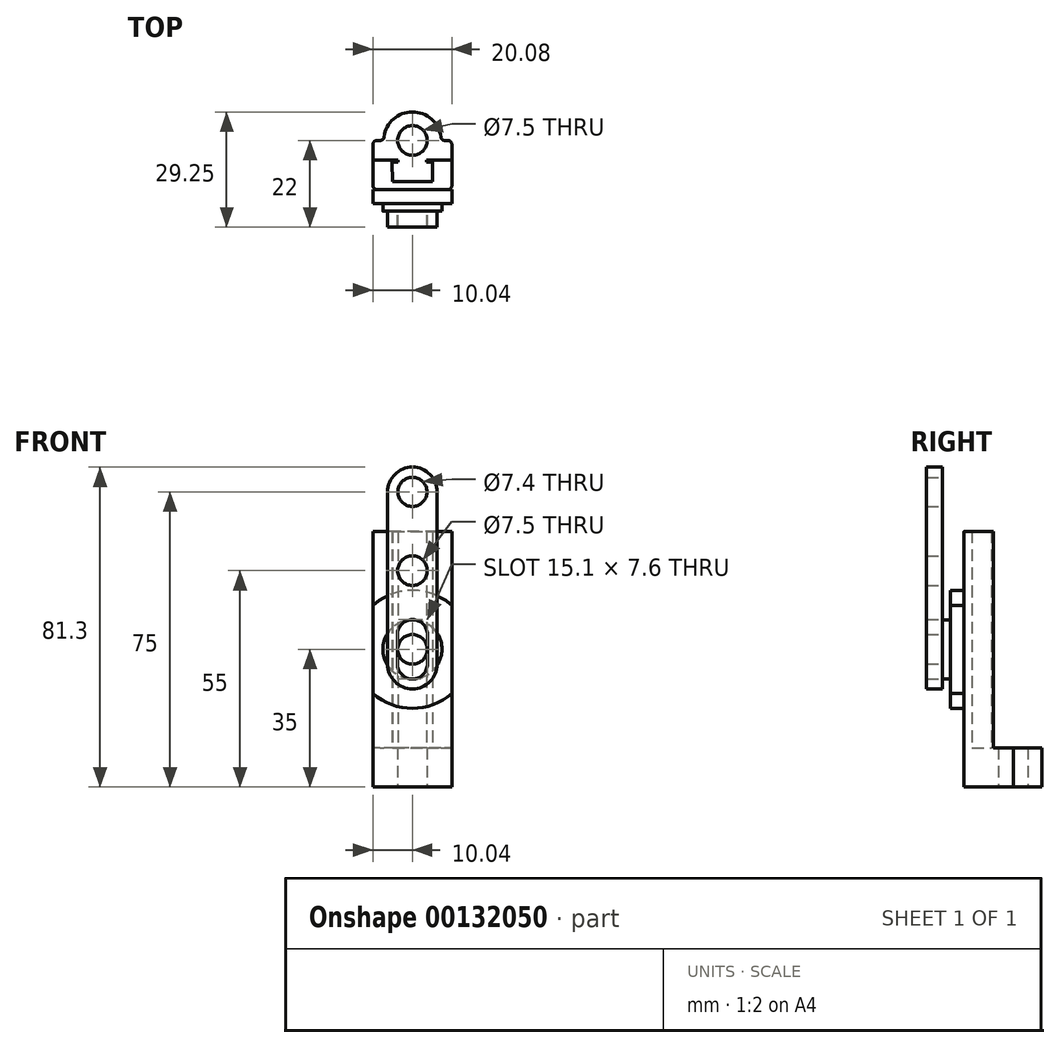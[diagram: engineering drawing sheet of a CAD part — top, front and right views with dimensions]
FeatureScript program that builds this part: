
annotation { "Feature Type Name" : "Feature", "Feature Type Description" : "" }
export const myFeature = defineFeature(function(context is Context, id is Id, definition is map)
    precondition{}
    {
        {
            var Q0;
            Q0=qCreatedBy(makeId("Top.planeOp"),FACE);
            var sketch = newSketch(context, id + "F0", { "sketchPlane" : qUnion([Q0])});
            skCircle(sketch, "E0", {"center": v(0, 0) * mm, "radius": 3.75 * mm});
            skArc(sketch, "E1.0", {"start": v(7.2, 0.88) * mm, "mid": v(0, 7.25) * mm, "end": v(-7.2, 0.88) * mm});
            skLineSegment(sketch, "E2.bottom", {"start": v(9, 0) * mm, "end": v(8.19, 0) * mm});
            skLineSegment(sketch, "E2.top", {"start": v(9, -12.5) * mm, "end": v(-9, -12.5) * mm});
            skLineSegment(sketch, "E2.left", {"start": v(10, -1) * mm, "end": v(10, -11.5) * mm});
            skLineSegment(sketch, "E2.right", {"start": v(-10, -1) * mm, "end": v(-10, -11.5) * mm});
            skLineSegment(sketch, "E3.trimOffspring", {"start": v(-8.19, 0) * mm, "end": v(-9, 0) * mm});
            skPoint(sketch, "E4.visualSharp", {"position": v(-7.25, 0) * mm});
            skArc(sketch, "E4.filletArc", {"start": v(-8.19, 0) * mm, "mid": v(-7.53, 0.25) * mm, "end": v(-7.2, 0.88) * mm});
            skPoint(sketch, "E5.visualSharp", {"position": v(7.25, 0) * mm});
            skArc(sketch, "E5.filletArc", {"start": v(7.2, 0.88) * mm, "mid": v(7.53, 0.25) * mm, "end": v(8.19, 0) * mm});
            skPoint(sketch, "E6.visualSharp", {"position": v(10, 0) * mm});
            skArc(sketch, "E6.filletArc", {"start": v(10, -1) * mm, "mid": v(9.7, -0.3) * mm, "end": v(9, 0) * mm});
            skPoint(sketch, "E7.visualSharp", {"position": v(-10, 0) * mm});
            skArc(sketch, "E7.filletArc", {"start": v(-9, 0) * mm, "mid": v(-9.7, -0.3) * mm, "end": v(-10, -1) * mm});
            skPoint(sketch, "E8.visualSharp", {"position": v(10, -12.5) * mm});
            skArc(sketch, "E8.filletArc", {"start": v(9, -12.5) * mm, "mid": v(9.7, -12.2) * mm, "end": v(10, -11.5) * mm});
            skPoint(sketch, "E9.visualSharp", {"position": v(-10, -12.5) * mm});
            skArc(sketch, "E9.filletArc", {"start": v(-10, -11.5) * mm, "mid": v(-9.7, -12.2) * mm, "end": v(-9, -12.5) * mm});
            skSolve(sketch);
        }
        {
            var Q0;
            Q0=makeQuery(id+"F0.imprint","IMPRINT",FACE,{"disambiguationData":[TD([[makeQuery(id+"F0.imprint","IMPRINT",EDGE,{"derivedFrom":sQuery(id+"F0.wireOp",EDGE,"E0")}),-1.0]])]});
            extrude(context, id + "F1", {"entities" : qUnion([Q0]), "depth" : 10 * mm});
        }
        {
            var Q0;
            Q0=makeQuery(id+"F1.opExtrude","CAP_FACE",FACE,{"disambiguationData":[OSD([sQuery(id+"F0.wireOp",EDGE,"E0"),sQuery(id+"F0.wireOp",EDGE,"E1.0"),sQuery(id+"F0.wireOp",EDGE,"E2.bottom"),sQuery(id+"F0.wireOp",EDGE,"E2.top"),sQuery(id+"F0.wireOp",EDGE,"E2.left"),sQuery(id+"F0.wireOp",EDGE,"E2.right"),sQuery(id+"F0.wireOp",EDGE,"E3.trimOffspring"),sQuery(id+"F0.wireOp",EDGE,"E4.filletArc"),sQuery(id+"F0.wireOp",EDGE,"E5.filletArc"),sQuery(id+"F0.wireOp",EDGE,"E6.filletArc"),sQuery(id+"F0.wireOp",EDGE,"E7.filletArc"),sQuery(id+"F0.wireOp",EDGE,"E8.filletArc"),sQuery(id+"F0.wireOp",EDGE,"E9.filletArc")])],"isStart":false});
            var sketch = newSketch(context, id + "F2", { "sketchPlane" : qUnion([Q0])});
            skLineSegment(sketch, "E10", {"start": v(3.6, -5) * mm, "end": v(10, -5) * mm});
            skLineSegment(sketch, "E11", {"start": v(10, -5) * mm, "end": v(10, -11.5) * mm});
            skPoint(sketch, "E12.visualSharp", {"position": v(10, -12.5) * mm});
            skArc(sketch, "E12.filletArc", {"start": v(9, -12.5) * mm, "mid": v(9.7, -12.2) * mm, "end": v(10, -11.5) * mm});
            skLineSegment(sketch, "E13.MirrorCS", {"start": v(-10, -5) * mm, "end": v(-10, -11.5) * mm});
            skArc(sketch, "E14.MirrorCS", {"start": v(-9, -12.5) * mm, "mid": v(-9.7, -12.2) * mm, "end": v(-10, -11.5) * mm});
            skLineSegment(sketch, "E15", {"start": v(-9, -12.5) * mm, "end": v(9, -12.5) * mm});
            skLineSegment(sketch, "E16", {"start": v(3.6, -5) * mm, "end": v(3.6, -5.5) * mm});
            skLineSegment(sketch, "E17", {"start": v(3.6, -5.5) * mm, "end": v(5.14, -5.5) * mm});
            skPoint(sketch, "E18.orphan", {"position": v(0, -5) * mm});
            skLineSegment(sketch, "E19", {"start": v(5.05, -10.5) * mm, "end": v(5.14, -5.5) * mm});
            skLineSegment(sketch, "E20.MirrorCS", {"start": v(-5.05, -10.5) * mm, "end": v(-5.14, -5.5) * mm});
            skLineSegment(sketch, "E21.MirrorCS", {"start": v(-3.6, -5.5) * mm, "end": v(-5.14, -5.5) * mm});
            skLineSegment(sketch, "E22.MirrorCS", {"start": v(-3.6, -5) * mm, "end": v(-10, -5) * mm});
            skLineSegment(sketch, "E23.MirrorCS", {"start": v(-3.6, -5) * mm, "end": v(-3.6, -5.5) * mm});
            skLineSegment(sketch, "E24", {"start": v(-5.05, -10.5) * mm, "end": v(5.05, -10.5) * mm});
            skSolve(sketch);
        }
        {
            var Q0;
            Q0 = qSketchRegion(id + "F2", true);
            extrude(context, id + "F3", {"entities" : qUnion([Q0]), "operationType" : NewBodyOperationType.ADD, "depth" : 55 * mm});
        }
        {
            var Q0;
            Q0=makeQuery(id+"F3.boolean.opBoolean","MERGE",FACE,{"derivedFrom":[makeQuery(id+"F1.opExtrude","SWEPT_FACE",FACE,{"disambiguationData":[OSD([sQuery(id+"F0.wireOp",EDGE,"E2.top")])]}),makeQuery(id+"F3.opExtrude","SWEPT_FACE",FACE,{"disambiguationData":[OSD([sQuery(id+"F2.wireOp",EDGE,"rY1W6HYS-8gYD-yjMk-udCq-DS8X7DJZpoX9")])]}),makeQuery(id+"F3.opExtrude","SWEPT_FACE",FACE,{"disambiguationData":[OSD([sQuery(id+"F2.wireOp",EDGE,"4e3df5a9-557a-405f-80d9-8388369b6b7d0.MirrorCS")])]})]});
            var sketch = newSketch(context, id + "F4", { "sketchPlane" : qUnion([Q0])});
            skLineSegment(sketch, "E25", {"start": v(0, 0) * mm, "end": v(0, 35) * mm});
            skArc(sketch, "E26", {"start": v(10.04, 46.14) * mm, "mid": v(0, 50) * mm, "end": v(-10.04, 46.14) * mm});
            skLineSegment(sketch, "E27", {"start": v(10.04, 46.14) * mm, "end": v(10.04, 23.86) * mm});
            skLineSegment(sketch, "E28.MirrorCS", {"start": v(-10.04, 46.14) * mm, "end": v(-10.04, 23.86) * mm});
            skPoint(sketch, "E29.orphan", {"position": v(10.04, 48.03) * mm});
            skPoint(sketch, "E30.orphan", {"position": v(10.04, 18.64) * mm});
            skPoint(sketch, "E31.orphan", {"position": v(-10.04, 48.03) * mm});
            skPoint(sketch, "E32.orphan", {"position": v(-10.04, 18.64) * mm});
            skArc(sketch, "E33.trimOffspring", {"start": v(-10.04, 23.86) * mm, "mid": v(0, 20) * mm, "end": v(10.04, 23.86) * mm});
            skSolve(sketch);
        }
        {
            var Q0;
            Q0 = qSketchRegion(id + "F4", true);
            extrude(context, id + "F5", {"entities" : qUnion([Q0]), "depth" : 3.5 * mm});
        }
        {
            var Q0;
            Q0=makeQuery(id+"F5.opExtrude","CAP_FACE",FACE,{"disambiguationData":[OSD([sQuery(id+"F4.wireOp",EDGE,"E26"),sQuery(id+"F4.wireOp",EDGE,"E27"),sQuery(id+"F4.wireOp",EDGE,"E28.MirrorCS"),sQuery(id+"F4.wireOp",EDGE,"E33.trimOffspring")])],"isStart":false});
            var sketch = newSketch(context, id + "F6", { "sketchPlane" : qUnion([Q0])});
            skCircle(sketch, "E34", {"center": v(0, 35) * mm, "radius": 7.5 * mm});
            skSolve(sketch);
        }
        {
            var Q0;
            Q0=makeQuery(id+"F6.imprint","IMPRINT",FACE,{"disambiguationData":[TD([[makeQuery(id+"F6.imprint","IMPRINT",EDGE,{"derivedFrom":sQuery(id+"F6.wireOp",EDGE,"E34")}),1.0]])]});
            extrude(context, id + "F7", {"entities" : qUnion([Q0]), "operationType" : NewBodyOperationType.ADD, "depth" : 2 * mm});
        }
        {
            var Q0;
            Q0=makeQuery(id+"F7.opExtrude","CAP_FACE",FACE,{"disambiguationData":[OSD([sQuery(id+"F6.wireOp",EDGE,"E34")])],"isStart":false});
            var sketch = newSketch(context, id + "F8", { "sketchPlane" : qUnion([Q0])});
            skCircle(sketch, "E35", {"center": v(0, 35) * mm, "radius": 3.75 * mm});
            skLineSegment(sketch, "E36.left", {"start": v(-3.8, 38.75) * mm, "end": v(-3.8, 31.25) * mm});
            skLineSegment(sketch, "E36.right", {"start": v(3.8, 38.75) * mm, "end": v(3.8, 31.25) * mm});
            skArc(sketch, "E37", {"start": v(3.8, 38.75) * mm, "mid": v(0, 42.55) * mm, "end": v(-3.8, 38.75) * mm});
            skArc(sketch, "E38", {"start": v(-3.8, 31.25) * mm, "mid": v(0, 27.45) * mm, "end": v(3.8, 31.25) * mm});
            skArc(sketch, "E39.0", {"start": v(-6.3, 31.25) * mm, "mid": v(0, 24.95) * mm, "end": v(6.3, 31.25) * mm});
            skLineSegment(sketch, "E40.bottom", {"start": v(3.8, 35) * mm, "end": v(3.75, 35) * mm});
            skLineSegment(sketch, "E40.top", {"start": v(6.3, 55) * mm, "end": v(6.25, 55) * mm});
            skLineSegment(sketch, "E41", {"start": v(-6.3, 55) * mm, "end": v(-6.3, 31.25) * mm});
            skLineSegment(sketch, "E42", {"start": v(6.3, 55) * mm, "end": v(6.3, 31.25) * mm});
            skLineSegment(sketch, "E43.left", {"start": v(6.3, 55) * mm, "end": v(6.3, 75) * mm});
            skLineSegment(sketch, "E43.right", {"start": v(-6.3, 55) * mm, "end": v(-6.3, 75) * mm});
            skCircle(sketch, "E44", {"center": v(0, 55) * mm, "radius": 3.75 * mm});
            skLineSegment(sketch, "E45.trimOffspring", {"start": v(-6.25, 55) * mm, "end": v(-6.3, 55) * mm});
            skArc(sketch, "E46", {"start": v(6.3, 75) * mm, "mid": v(0, 81.3) * mm, "end": v(-6.3, 75) * mm});
            skCircle(sketch, "E47", {"center": v(0, 75) * mm, "radius": 3.7 * mm});
            skLineSegment(sketch, "E48.trimOffspring", {"start": v(-3.75, 35) * mm, "end": v(-3.8, 35) * mm});
            skSolve(sketch);
        }
        {
            var Q0;
            Q0=makeQuery(id+"F8.imprint","IMPRINT",FACE,{"disambiguationData":[TD([[makeQuery(id+"F8.imprint","IMPRINT",EDGE,{"derivedFrom":sQuery(id+"F8.wireOp",EDGE,"E35")}),1.0]])]});
            extrude(context, id + "F9", {"entities" : qUnion([Q0]), "operationType" : NewBodyOperationType.ADD, "depth" : 4 * mm});
        }
        {
            var Q0;
            Q0 = qSketchRegion(id + "F8", true);
            extrude(context, id + "F10", {"entities" : qUnion([Q0]), "depth" : 4 * mm});
        }
    });
